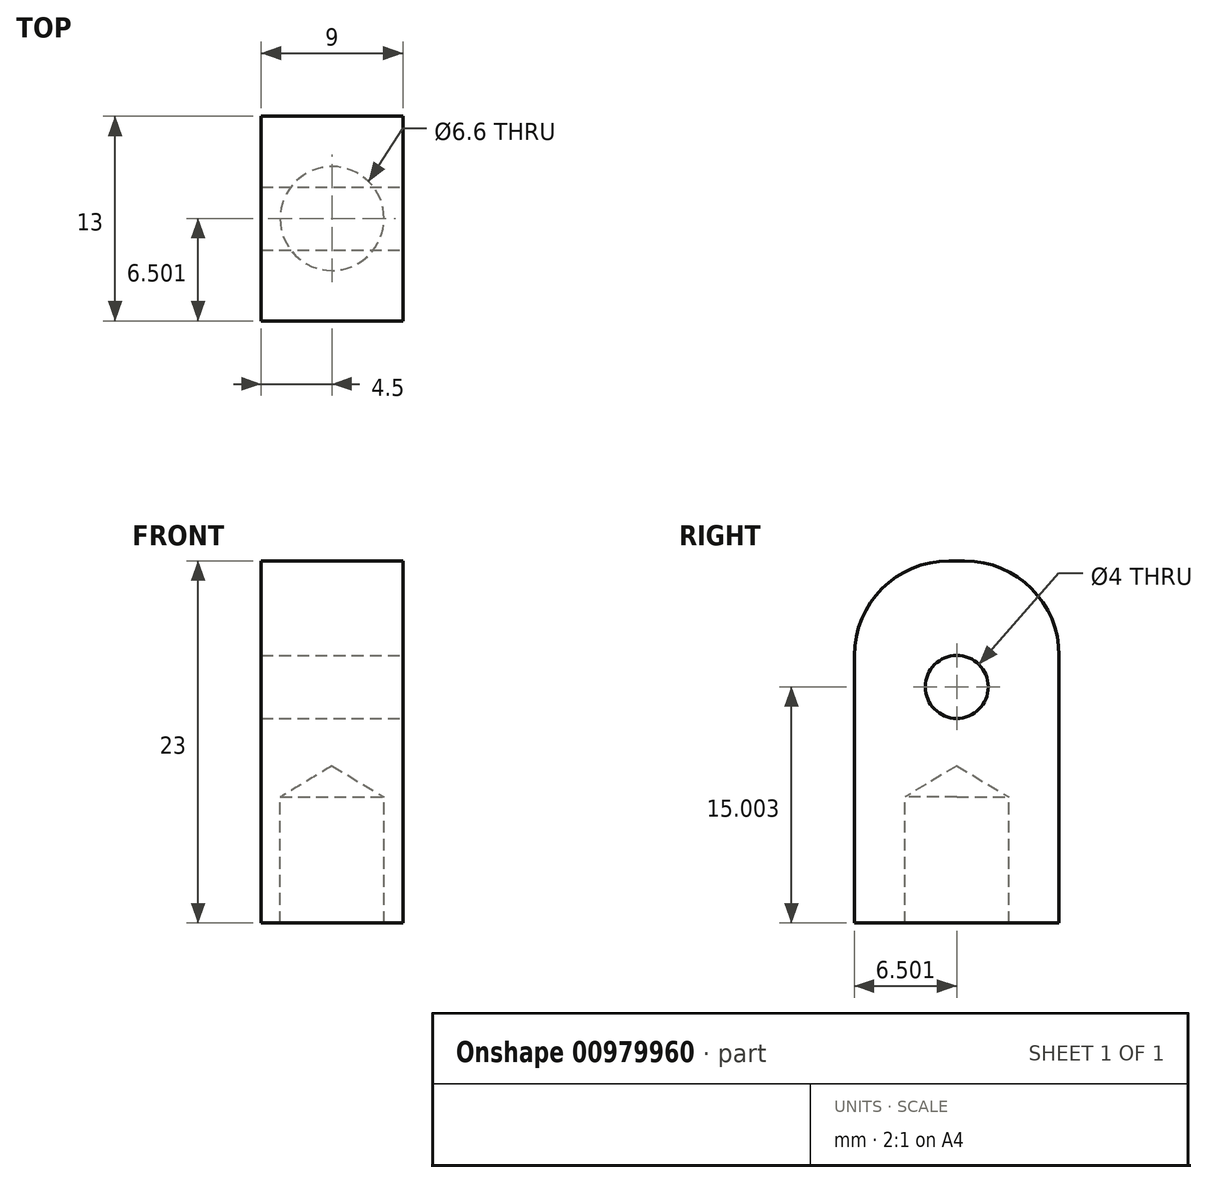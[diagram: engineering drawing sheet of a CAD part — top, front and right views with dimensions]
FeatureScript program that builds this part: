
annotation { "Feature Type Name" : "Feature", "Feature Type Description" : "" }
export const myFeature = defineFeature(function(context is Context, id is Id, definition is map)
    precondition{}
    {
        {
            var Q0;
            Q0=qCreatedBy(makeId("Right.planeOp"),FACE);
            var sketch = newSketch(context, id + "F0", { "sketchPlane" : qUnion([Q0])});
            skLineSegment(sketch, "E0", {"start": v(-3.2, -10.08) * mm, "end": v(9.8, -10.08) * mm});
            skLineSegment(sketch, "E1", {"start": v(9.8, -10.08) * mm, "end": v(9.8, 12.92) * mm});
            skLineSegment(sketch, "E2", {"start": v(9.8, 12.92) * mm, "end": v(-3.2, 12.92) * mm});
            skLineSegment(sketch, "E3", {"start": v(-3.2, 12.92) * mm, "end": v(-3.2, -10.08) * mm});
            skSolve(sketch);
        }
        {
            var Q0;
            Q0 = qSketchRegion(id + "F0", true);
            extrude(context, id + "F1", {"entities" : qUnion([Q0]), "depth" : 9 * mm, "offsetDistance" : 25.4 * mm});
        }
        {
            var Q0;
            Q0=makeQuery(id+"F1.opExtrude","SWEPT_EDGE",EDGE,{"disambiguationData":[OSD([sQuery(id+"F0.wireOp",EDGE,"E2"),sQuery(id+"F0.wireOp",EDGE,"E3")])]});
            var Q1;
            Q1=makeQuery(id+"F1.opExtrude","SWEPT_EDGE",EDGE,{"disambiguationData":[OSD([sQuery(id+"F0.wireOp",EDGE,"E1"),sQuery(id+"F0.wireOp",EDGE,"E2")])]});
            fillet(context, id + "F2", {"entities" : qUnion([Q0, Q1]), "radius" : 6 * mm, "tangentPropagation" : true, "allowEdgeOverflow" : false});
        }
        {
            var Q0;
            Q0=makeQuery(id+"F1.opExtrude","CAP_FACE",FACE,{"disambiguationData":[OSD([sQuery(id+"F0.wireOp",EDGE,"E0"),sQuery(id+"F0.wireOp",EDGE,"E1"),sQuery(id+"F0.wireOp",EDGE,"E2"),sQuery(id+"F0.wireOp",EDGE,"E3")])],"isStart":false});
            var sketch = newSketch(context, id + "F3", { "sketchPlane" : qUnion([Q0])});
            skLineSegment(sketch, "E4", {"start": v(3.3, 13.78) * mm, "end": v(3.3, -13.12) * mm});
            skPoint(sketch, "E4.startSnap0", {"position": v(3.3, 12.92) * mm});
            skCircle(sketch, "E5", {"center": v(3.3, 4.92) * mm, "radius": 2 * mm});
            skSolve(sketch);
        }
        {
            var Q0;
            Q0 = qSketchRegion(id + "F3", true);
            extrude(context, id + "F4", {"entities" : qUnion([Q0]), "operationType" : NewBodyOperationType.REMOVE, "endBound" : BoundingType.THROUGH_ALL, "oppositeDirection" : true, "depth" : 25.4 * mm, "offsetDistance" : 25.4 * mm});
        }
        {
            var Q0;
            Q0=makeQuery(id+"F1.opExtrude","SWEPT_FACE",FACE,{"disambiguationData":[OSD([sQuery(id+"F0.wireOp",EDGE,"E0")])]});
            var sketch = newSketch(context, id + "F5", { "sketchPlane" : qUnion([Q0])});
            skLineSegment(sketch, "E6", {"start": v(11.15, -3.3) * mm, "end": v(-3.01, -3.3) * mm});
            skPoint(sketch, "E6.startSnap0", {"position": v(9, -3.3) * mm});
            skPoint(sketch, "E6.endSnap0", {"position": v(0, -3.3) * mm});
            skLineSegment(sketch, "E7", {"start": v(4.5, 5.35) * mm, "end": v(4.5, -13.15) * mm});
            skPoint(sketch, "E7.startSnap0", {"position": v(4.5, 3.2) * mm});
            skPoint(sketch, "E8", {"position": v(4.5, -3.3) * mm});
            skSolve(sketch);
        }
        {
            var Q0;
            Q0=sQuery(id+"F5.wireOp",VERTEX,"E8");
            var Q1;
            Q1=makeQuery(id+"F1.opExtrude","SWEPT_BODY",BODY,{"disambiguationData":[OSD([sQuery(id+"F0.wireOp",EDGE,"E0"),sQuery(id+"F0.wireOp",EDGE,"E1"),sQuery(id+"F0.wireOp",EDGE,"E2"),sQuery(id+"F0.wireOp",EDGE,"E3")])]});
            hole(context, id + "F6", {"style" : HoleStyle.SIMPLE, "endStyle" : HoleEndStyle.BLIND, "standardTappedOrClearance" : lookupTablePath({ "fit" : "Normal", "standard" : "ISO", "size" : "M6", "type" : "Clearance" }), "standardBlindInLast" : lookupTablePath({ "fit" : "Normal", "standard" : "ISO", "engagement" : "75%", "pitch" : "1 mm", "size" : "M6", "type" : "Clearance & tapped" }), "holeDiameter" : 6.6 * mm, "majorDiameter" : 6.35 * mm, "holeDepth" : 8 * mm, "isTappedThrough" : true, "tappedDepth" : 12.7 * mm, "tapClearance" : 3, "locations" : qUnion([Q0]), "scope" : qUnion([Q1]), "startStyle" : HoleStartStyle.PART});
        }
    });
